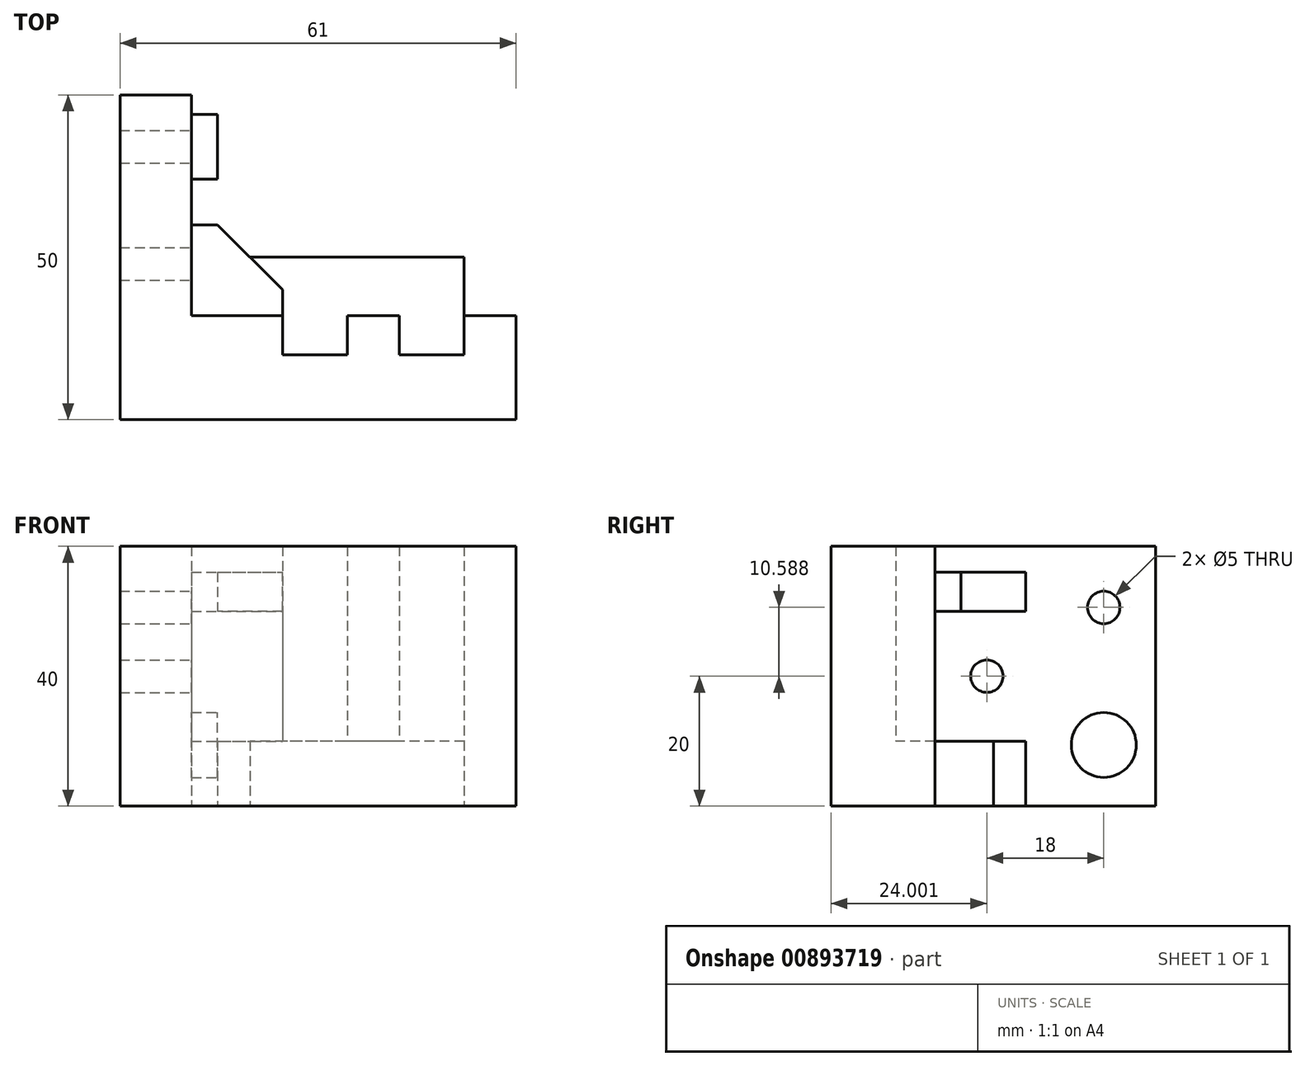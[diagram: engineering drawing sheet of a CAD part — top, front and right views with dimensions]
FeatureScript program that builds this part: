
annotation { "Feature Type Name" : "Feature", "Feature Type Description" : "" }
export const myFeature = defineFeature(function(context is Context, id is Id, definition is map)
    precondition{}
    {
        {
            var Q0;
            Q0=qCreatedBy(makeId("Top.planeOp"),FACE);
            var sketch = newSketch(context, id + "F0", { "sketchPlane" : qUnion([Q0])});
            skLineSegment(sketch, "E0", {"start": v(-20.9, 37.61) * mm, "end": v(-35.9, 37.61) * mm});
            skLineSegment(sketch, "E1", {"start": v(-35.9, 37.61) * mm, "end": v(-35.9, -12.39) * mm});
            skLineSegment(sketch, "E2", {"start": v(-35.9, -12.39) * mm, "end": v(25.1, -12.39) * mm});
            skLineSegment(sketch, "E3", {"start": v(25.1, -12.39) * mm, "end": v(25.1, 3.61) * mm});
            skLineSegment(sketch, "E4", {"start": v(25.1, 3.61) * mm, "end": v(17.1, 3.61) * mm});
            skLineSegment(sketch, "E5", {"start": v(17.1, 3.61) * mm, "end": v(17.1, -2.39) * mm});
            skLineSegment(sketch, "E6", {"start": v(17.1, -2.39) * mm, "end": v(7.1, -2.39) * mm});
            skLineSegment(sketch, "E7", {"start": v(7.1, -2.39) * mm, "end": v(7.1, 3.61) * mm});
            skLineSegment(sketch, "E8", {"start": v(7.1, 3.61) * mm, "end": v(-0.9, 3.61) * mm});
            skLineSegment(sketch, "E9", {"start": v(-0.9, 3.61) * mm, "end": v(-0.9, -2.39) * mm});
            skLineSegment(sketch, "E10", {"start": v(-0.9, -2.39) * mm, "end": v(-10.9, -2.39) * mm});
            skLineSegment(sketch, "E11", {"start": v(-10.9, -2.39) * mm, "end": v(-10.9, 3.61) * mm});
            skLineSegment(sketch, "E12", {"start": v(-10.9, 3.61) * mm, "end": v(-20.9, 3.61) * mm});
            skLineSegment(sketch, "E13", {"start": v(-20.9, 3.61) * mm, "end": v(-20.9, 37.61) * mm});
            skSolve(sketch);
        }
        {
            var Q0;
            Q0=makeQuery(id+"F0.imprint","IMPRINT",FACE,{"disambiguationData":[TD([[makeQuery(id+"F0.imprint","IMPRINT",EDGE,{"derivedFrom":sQuery(id+"F0.wireOp",EDGE,"E0")}),1.0]])]});
            extrude(context, id + "F1", {"entities" : qUnion([Q0]), "depth" : 40 * mm, "offsetDistance" : 25 * mm});
        }
        {
            var Q0;
            Q0=makeQuery(id+"F1.opExtrude","SWEPT_FACE",FACE,{"disambiguationData":[OSD([sQuery(id+"F0.wireOp",EDGE,"E13")])]});
            var sketch = newSketch(context, id + "F2", { "sketchPlane" : qUnion([Q0])});
            skLineSegment(sketch, "E14", {"start": v(37.61, 40) * mm, "end": v(3.61, 0) * mm, "construction": true});
            skLineSegment(sketch, "E15", {"start": v(20.61, 20) * mm, "end": v(11.61, 20) * mm, "construction": true});
            skLineSegment(sketch, "E16", {"start": v(20.61, 20) * mm, "end": v(29.61, 20) * mm, "construction": true});
            skLineSegment(sketch, "E17", {"start": v(29.61, 20) * mm, "end": v(29.61, 30.59) * mm, "construction": true});
            skLineSegment(sketch, "E18.MirrorCS", {"start": v(29.61, 20) * mm, "end": v(29.61, 9.41) * mm, "construction": true});
            skCircle(sketch, "E19", {"center": v(29.61, 30.59) * mm, "radius": 5 * mm});
            skCircle(sketch, "E20.0", {"center": v(29.61, 30.59) * mm, "radius": 2.5 * mm});
            skCircle(sketch, "E21.MirrorC", {"center": v(29.61, 9.41) * mm, "radius": 5 * mm});
            skCircle(sketch, "E22.MirrorC", {"center": v(29.61, 9.41) * mm, "radius": 2.5 * mm});
            skCircle(sketch, "E23", {"center": v(11.61, 20) * mm, "radius": 5 * mm});
            skCircle(sketch, "E24.0", {"center": v(11.61, 20) * mm, "radius": 2.5 * mm});
            skLineSegment(sketch, "E25.bottom", {"start": v(3.61, 36) * mm, "end": v(17.61, 36) * mm});
            skLineSegment(sketch, "E25.top", {"start": v(3.61, 30) * mm, "end": v(17.61, 30) * mm});
            skLineSegment(sketch, "E25.left", {"start": v(3.61, 36) * mm, "end": v(3.61, 30) * mm});
            skLineSegment(sketch, "E25.right", {"start": v(17.61, 36) * mm, "end": v(17.61, 30) * mm});
            skLineSegment(sketch, "E26.MirrorCS", {"start": v(3.61, 10) * mm, "end": v(17.61, 10) * mm});
            skLineSegment(sketch, "E27", {"start": v(17.61, 10) * mm, "end": v(17.61, 0) * mm});
            skLineSegment(sketch, "E28", {"start": v(17.61, 0) * mm, "end": v(3.61, 0) * mm});
            skSolve(sketch);
        }
        {
            var Q0;
            Q0=makeQuery(id+"F2.imprint","IMPRINT",FACE,{"disambiguationData":[TD([[makeQuery(id+"F2.imprint","IMPRINT",EDGE,{"derivedFrom":sQuery(id+"F2.wireOp",EDGE,"E21.MirrorC")}),-1.0]])]});
            var Q1;
            Q1=makeQuery(id+"F2.imprint","IMPRINT",FACE,{"disambiguationData":[TD([[makeQuery(id+"F2.imprint","IMPRINT",EDGE,{"derivedFrom":sQuery(id+"F2.wireOp",EDGE,"E23")}),1.0]])]});
            var Q2;
            Q2=makeQuery(id+"F2.imprint","IMPRINT",FACE,{"disambiguationData":[TD([[makeQuery(id+"F2.imprint","IMPRINT",EDGE,{"derivedFrom":sQuery(id+"F2.wireOp",EDGE,"E19")}),1.0]])]});
            extrude(context, id + "F3", {"entities" : qUnion([Q0, Q1, Q2]), "operationType" : NewBodyOperationType.REMOVE, "oppositeDirection" : true, "depth" : 4 * mm, "offsetDistance" : 25 * mm});
        }
        {
            var Q0;
            Q0=makeQuery(id+"F3.boolean.opBoolean","SPLIT",FACE,{"disambiguationData":[TD([makeQuery(id+"F3.opExtrude","SWEPT_FACE",FACE,{"disambiguationData":[OSD([sQuery(id+"F2.wireOp",EDGE,"E22.MirrorC")])]})])],"derivedFrom":makeQuery(id+"F1.opExtrude","SWEPT_FACE",FACE,{"disambiguationData":[OSD([sQuery(id+"F0.wireOp",EDGE,"E13")])]})});
            var Q1;
            Q1=makeQuery(id+"F3.boolean.opBoolean","SPLIT",FACE,{"disambiguationData":[TD([makeQuery(id+"F3.opExtrude","SWEPT_FACE",FACE,{"disambiguationData":[OSD([sQuery(id+"F2.wireOp",EDGE,"E24.0")])]})])],"derivedFrom":makeQuery(id+"F1.opExtrude","SWEPT_FACE",FACE,{"disambiguationData":[OSD([sQuery(id+"F0.wireOp",EDGE,"E13")])]})});
            var Q2;
            Q2=makeQuery(id+"F3.boolean.opBoolean","SPLIT",FACE,{"disambiguationData":[TD([makeQuery(id+"F3.opExtrude","SWEPT_FACE",FACE,{"disambiguationData":[OSD([sQuery(id+"F2.wireOp",EDGE,"E20.0")])]})])],"derivedFrom":makeQuery(id+"F1.opExtrude","SWEPT_FACE",FACE,{"disambiguationData":[OSD([sQuery(id+"F0.wireOp",EDGE,"E13")])]})});
            extrude(context, id + "F4", {"entities" : qUnion([Q0, Q1, Q2]), "operationType" : NewBodyOperationType.REMOVE, "endBound" : BoundingType.THROUGH_ALL, "oppositeDirection" : true, "depth" : 25 * mm, "offsetDistance" : 25 * mm});
        }
        {
            var Q0;
            Q0=makeQuery(id+"F2.imprint","IMPRINT",FACE,{"disambiguationData":[TD([[makeQuery(id+"F2.imprint","IMPRINT",EDGE,{"derivedFrom":sQuery(id+"F2.wireOp",EDGE,"E25.bottom")}),-1.0]])]});
            var Q1;
            Q1=makeQuery(id+"F2.imprint","IMPRINT",FACE,{"disambiguationData":[TD([[makeQuery(id+"F2.imprint","IMPRINT",EDGE,{"derivedFrom":sQuery(id+"F2.wireOp",EDGE,"81b55ab7-f230-43ce-84fe-03862dbb9f280.MirrorCS")}),1.0]])]});
            extrude(context, id + "F5", {"entities" : qUnion([Q0, Q1]), "operationType" : NewBodyOperationType.ADD, "depth" : 10 * mm, "offsetDistance" : 25 * mm});
        }
        {
            var Q0;
            {var subQ0=sQuery(id+"F2.wireOp",EDGE,"E26.MirrorCS");Q0=makeQuery(id+"F2.imprint","IMPRINT",FACE,{"disambiguationData":[TD([[makeQuery(id+"F2.imprint","IMPRINT",EDGE,{"derivedFrom":subQ0}),-1.0]])]});}
            extrude(context, id + "F6", {"entities" : qUnion([Q0]), "operationType" : NewBodyOperationType.ADD, "depth" : 10 * mm, "offsetDistance" : 25 * mm});
        }
        {
            var Q0;
            Q0=makeQuery(id+"F5.opExtrude","CAP_EDGE",EDGE,{"disambiguationData":[OSD([sQuery(id+"F2.wireOp",EDGE,"E25.right")])],"isStart":false});
            chamfer(context, id + "F7", {"entities" : qUnion([Q0]), "width" : 10 * mm, "tangentPropagation" : true});
        }
        {
            var Q0;
            Q0=makeQuery(id+"F1.opExtrude","SWEPT_FACE",FACE,{"disambiguationData":[OSD([sQuery(id+"F0.wireOp",EDGE,"E10")])]});
            var sketch = newSketch(context, id + "F8", { "sketchPlane" : qUnion([Q0])});
            skLineSegment(sketch, "E29.bottom", {"start": v(-17.1, 0) * mm, "end": v(-7.1, 0) * mm});
            skLineSegment(sketch, "E29.top", {"start": v(-17.1, 10) * mm, "end": v(-7.1, 10) * mm});
            skLineSegment(sketch, "E29.left", {"start": v(-17.1, 0) * mm, "end": v(-17.1, 10) * mm});
            skLineSegment(sketch, "E29.right", {"start": v(-7.1, 0) * mm, "end": v(-7.1, 10) * mm});
            skLineSegment(sketch, "E30.bottom", {"start": v(0.9, 0) * mm, "end": v(10.9, 0) * mm});
            skLineSegment(sketch, "E30.top", {"start": v(0.9, 10) * mm, "end": v(10.9, 10) * mm});
            skLineSegment(sketch, "E30.left", {"start": v(0.9, 0) * mm, "end": v(0.9, 10) * mm});
            skLineSegment(sketch, "E30.right", {"start": v(10.9, 0) * mm, "end": v(10.9, 10) * mm});
            skLineSegment(sketch, "E31", {"start": v(0.9, 10) * mm, "end": v(-7.1, 10) * mm});
            skLineSegment(sketch, "E32", {"start": v(0.9, 0) * mm, "end": v(-7.1, 0) * mm});
            skSolve(sketch);
        }
        {
            var Q0;
            Q0=makeQuery(id+"F8.imprint","IMPRINT",FACE,{"disambiguationData":[TD([[makeQuery(id+"F8.imprint","IMPRINT",EDGE,{"derivedFrom":sQuery(id+"F8.wireOp",EDGE,"E29.bottom")}),1.0]])]});
            var Q1;
            Q1=makeQuery(id+"F8.imprint","IMPRINT",FACE,{"disambiguationData":[TD([[makeQuery(id+"F8.imprint","IMPRINT",EDGE,{"derivedFrom":sQuery(id+"F8.wireOp",EDGE,"E30.bottom")}),1.0]])]});
            var Q2;
            Q2=makeQuery(id+"F8.imprint","IMPRINT",FACE,{"disambiguationData":[TD([[makeQuery(id+"F8.imprint","IMPRINT",EDGE,{"derivedFrom":sQuery(id+"F8.wireOp",EDGE,"E29.right")}),-1.0]])]});
            extrude(context, id + "F9", {"entities" : qUnion([Q0, Q1, Q2]), "operationType" : NewBodyOperationType.ADD, "depth" : 15 * mm, "offsetDistance" : 25 * mm});
        }
        {
            var Q0;
            Q0=makeQuery(id+"F5.opExtrude","CAP_EDGE",EDGE,{"disambiguationData":[OSD([sQuery(id+"F2.wireOp",EDGE,"81b55ab7-f230-43ce-84fe-03862dbb9f280.MirrorCS")])],"isStart":false});
            var Q1;
            Q1=makeQuery(id+"F6.opExtrude","CAP_EDGE",EDGE,{"disambiguationData":[OSD([sQuery(id+"F2.wireOp",EDGE,"E27")])],"isStart":false});
            chamfer(context, id + "F10", {"entities" : qUnion([Q0, Q1]), "width" : 10 * mm, "tangentPropagation" : true});
        }
    });
